FCSTD DOCUMENT  (FreeCAD 0.22R37100 (Git))
Label: composit_stand10_model
License: All rights reserved
LicenseURL: http://en.wikipedia.org/wiki/All_rights_reserved
objects: App::Link×19, App::DocumentObjectGroup×3, PartDesign::CoordinateSystem×1, App::FeaturePython×1, App::Part×1
note: 1 computed .brp shape members not serialized (recipe doc carries the construction recipe); baked Part::Feature solids carry a one-line shape summary decoded from their .brp
EXTERNAL_REF file=composit_stand10.FCStd obj=Local_CS020
EXTERNAL_REF file=composit_stand10.FCStd obj=Body
EXTERNAL_REF file=composit_stand10.FCStd obj=Local_CS007
EXTERNAL_REF file=composit_stand10.FCStd obj=Local_CS010
EXTERNAL_REF file=composit_stand10.FCStd obj=Body001
EXTERNAL_REF file=composit_stand10.FCStd obj=Local_CS004
EXTERNAL_REF file=composit_stand10.FCStd obj=Local_CS005
EXTERNAL_REF file=composit_stand10.FCStd obj=Body012
EXTERNAL_REF file=composit_stand10.FCStd obj=Local_CS006
EXTERNAL_REF file=composit_stand10.FCStd obj=Local_CS012
EXTERNAL_REF file=composit_stand10.FCStd obj=Body003
EXTERNAL_REF file=composit_stand10.FCStd obj=Local_CS009
EXTERNAL_REF file=composit_stand10.FCStd obj=Local_CS015
EXTERNAL_REF file=composit_stand10.FCStd obj=Body010
EXTERNAL_REF file=composit_stand10.FCStd obj=Local_CS008
EXTERNAL_REF file=composit_stand10.FCStd obj=Local_CS013
EXTERNAL_REF file=composit_stand10.FCStd obj=Body006
EXTERNAL_REF file=composit_stand10.FCStd obj=Local_CS014
EXTERNAL_REF file=composit_stand10.FCStd obj=Local_CS016
EXTERNAL_REF file=composit_stand10.FCStd obj=Body004
EXTERNAL_REF file=composit_stand10.FCStd obj=Local_CS018
EXTERNAL_REF file=composit_stand10.FCStd obj=Body014
EXTERNAL_REF file=composit_stand10.FCStd obj=Local_CS025
EXTERNAL_REF file=composit_stand10.FCStd obj=Body011
EXTERNAL_REF file=composit_stand10.FCStd obj=Local_CS026
EXTERNAL_REF file=composit_stand10.FCStd obj=Local_CS027
EXTERNAL_REF file=composit_stand10.FCStd obj=Body019
EXTERNAL_REF file=composit_stand10.FCStd obj=Local_CS028
EXTERNAL_REF file=../magnet_fix.FCStd obj=Local_CS
EXTERNAL_REF file=../magnet_fix.FCStd obj=Body
EXTERNAL_REF file=composit_stand10.FCStd obj=LCS_1
EXTERNAL_REF file=composit_stand10.FCStd obj=Part
EXTERNAL_REF file=composit_stand10.FCStd obj=Local_CS029
EXTERNAL_REF file=composit_stand10.FCStd obj=Local_CS030
EXTERNAL_REF file=composit_stand10.FCStd obj=Body021
EXTERNAL_REF file=composit_stand10.FCStd obj=Local_CS031
EXTERNAL_REF file=composit_stand10.FCStd obj=Body024
EXTERNAL_REF file=../basin_2.FCStd obj=Local_CS
EXTERNAL_REF file=composit_stand10.FCStd obj=Local_CS022
EXTERNAL_REF file=../basin_2.FCStd obj=Body
EXTERNAL_REF file=composit_stand10.FCStd obj=Local_CS033
EXTERNAL_REF file=composit_stand10.FCStd obj=Body008
EXTERNAL_REF file=composit_stand10.FCStd obj=Local_CS032
EXTERNAL_REF file=composit_stand10.FCStd obj=Local_CS034
EXTERNAL_REF file=composit_stand10.FCStd obj=Body028
EXTERNAL_REF file=composit_stand10.FCStd obj=Local_CS035
EXTERNAL_REF file=../water_sensor.FCStd obj=Assembly
EXTERNAL_REF file=../composit_electric_shield.FCStd obj=Body
EXTERNAL_REF file=../composit_electric_shield.FCStd obj=Local_CS
EXTERNAL_REF file=composit_stand10.FCStd obj=Local_CS036

FEATURE [App::DocumentObjectGroup] Parts
FEATURE [PartDesign::CoordinateSystem] LCS_Origin
  AttacherType = Attacher::AttachEngine3D
  AttachmentSupport = -> [XY_Plane]
  MapMode = 2
FEATURE [App::DocumentObjectGroup] Constraints
FEATURE [App::FeaturePython] Variables  # WARN: FeaturePython — macro-defined, semantics opaque (R4)
  Type = App::PropertyContainer
FEATURE [App::DocumentObjectGroup] Configurations
FEATURE [App::Link] face
  AttachedBy = #Local_CS020
  AttachedTo = Parent Assembly#LCS_Origin
  AttachmentOffset = pos=(0,0,0) rot=(0,0,1;3.14159rad)
  LinkPlacement = pos=(0,0,0) rot=(0,0,1;3.14159rad)
  LinkedObject = -> <external composit_stand10.FCStd>#Body
  Placement = pos=(0,0,0) rot=(0,0,1;3.14159rad)
  SolverId = Asm4EE
  expr: Placement = LCS_Origin.Placement * AttachmentOffset * composit_stand10#Local_CS020.Placement ^ -1
FEATURE [App::Link] back
  AttachedBy = #Local_CS010
  AttachedTo = face#Local_CS007
  LinkPlacement = pos=(0,0,0) rot=(0,0,1;3.14159rad)
  LinkedObject = -> <external composit_stand10.FCStd>#Body001
  Placement = pos=(0,0,0) rot=(0,0,1;3.14159rad)
  SolverId = Asm4EE
  expr: Placement = face.Placement * composit_stand10#Local_CS007.Placement * AttachmentOffset * composit_stand10#Local_CS010.Placement ^ -1
FEATURE [App::Link] sink
  AttachedBy = #Local_CS004
  AttachedTo = face#Local_CS005
  LinkPlacement = pos=(-1.1e-14,-90,140) rot=(0,0,1;3.14159rad)
  LinkedObject = -> <external composit_stand10.FCStd>#Body012
  Placement = pos=(-1.1e-14,-90,140) rot=(0,0,1;3.14159rad)
  SolverId = Asm4EE
  expr: Placement = face.Placement * composit_stand10#Local_CS005.Placement * AttachmentOffset * composit_stand10#Local_CS004.Placement ^ -1
FEATURE [App::Link] lamp_holder
  AttachedBy = #Local_CS012
  AttachedTo = face#Local_CS006
  LinkPlacement = pos=(-1.1e-14,-90,254) rot=(0,0,1;3.14159rad)
  LinkedObject = -> <external composit_stand10.FCStd>#Body003
  Placement = pos=(-1.1e-14,-90,254) rot=(0,0,1;3.14159rad)
  SolverId = Asm4EE
  expr: Placement = face.Placement * composit_stand10#Local_CS006.Placement * AttachmentOffset * composit_stand10#Local_CS012.Placement ^ -1
FEATURE [App::Link] cap_outer
  AttachedBy = #Local_CS015
  AttachedTo = face#Local_CS009
  LinkPlacement = pos=(0,0,813) rot=(0,0,1;3.14159rad)
  LinkedObject = -> <external composit_stand10.FCStd>#Body010
  Placement = pos=(0,0,813) rot=(0,0,1;3.14159rad)
  SolverId = Asm4EE
  expr: Placement = face.Placement * composit_stand10#Local_CS009.Placement * AttachmentOffset * composit_stand10#Local_CS015.Placement ^ -1
FEATURE [App::Link] dropper_fix_composit
  AttachedBy = #Local_CS013
  AttachedTo = face#Local_CS008
  LinkPlacement = pos=(-1.1e-14,-90,813.1) rot=(0,0,1;3.14159rad)
  LinkedObject = -> <external composit_stand10.FCStd>#Body006
  Placement = pos=(-1.1e-14,-90,813.1) rot=(0,0,1;3.14159rad)
  SolverId = Asm4EE
  expr: Placement = face.Placement * composit_stand10#Local_CS008.Placement * AttachmentOffset * composit_stand10#Local_CS013.Placement ^ -1
FEATURE [App::Link] dropper_fix_PP
  AttachedBy = #Local_CS016
  AttachedTo = dropper_fix_composit#Local_CS014
  LinkPlacement = pos=(-1.1e-14,-90,816.1) rot=(0,0,1;3.14159rad)
  LinkedObject = -> <external composit_stand10.FCStd>#Body004
  Placement = pos=(-1.1e-14,-90,816.1) rot=(0,0,1;3.14159rad)
  SolverId = Asm4EE
  expr: Placement = dropper_fix_composit.Placement * composit_stand10#Local_CS014.Placement * AttachmentOffset * composit_stand10#Local_CS016.Placement ^ -1
FEATURE [App::Link] bottom_composit
  AttachedBy = #Local_CS018
  AttachedTo = face#Local_CS007
  LinkPlacement = pos=(0,0,0) rot=(0,0,1;3.14159rad)
  LinkedObject = -> <external composit_stand10.FCStd>#Body014
  Placement = pos=(0,0,0) rot=(0,0,1;3.14159rad)
  SolverId = Asm4EE
  expr: Placement = face.Placement * composit_stand10#Local_CS007.Placement * AttachmentOffset * composit_stand10#Local_CS018.Placement ^ -1
FEATURE [App::Link] cap_inner
  AttachedBy = #Local_CS025
  AttachedTo = cap_outer#Local_CS015
  LinkPlacement = pos=(0,0,813) rot=(0,0,1;3.14159rad)
  LinkedObject = -> <external composit_stand10.FCStd>#Body011
  Placement = pos=(0,0,813) rot=(0,0,1;3.14159rad)
  SolverId = Asm4EE
  expr: Placement = cap_outer.Placement * composit_stand10#Local_CS015.Placement * AttachmentOffset * composit_stand10#Local_CS025.Placement ^ -1
FEATURE [App::Link] magnet_fix
  AttachedBy = #Local_CS026
  AttachedTo = face#Local_CS027
  LinkPlacement = pos=(-299.78,-218,16) rot=(0,0,1;3.14159rad)
  LinkedObject = -> <external composit_stand10.FCStd>#Body019
  Placement = pos=(-299.78,-218,16) rot=(0,0,1;3.14159rad)
  SolverId = Asm4EE
  expr: Placement = face.Placement * composit_stand10#Local_CS027.Placement * AttachmentOffset * composit_stand10#Local_CS026.Placement ^ -1
FEATURE [App::Link] Body
  AttachedBy = #Local_CS
  AttachedTo = magnet_fix#Local_CS028
  LinkPlacement = pos=(-299.78,-210.7,36) rot=(-0.707107,0,-0.707107;3.14159rad)
  LinkedObject = -> <external ../magnet_fix.FCStd>#Body
  Placement = pos=(-299.78,-210.7,36) rot=(-0.707107,0,-0.707107;3.14159rad)
  SolverId = Asm4EE
  expr: Placement = magnet_fix.Placement * composit_stand10#Local_CS028.Placement * AttachmentOffset * magnet_fix#Local_CS.Placement ^ -1
FEATURE [App::Link] modules
  AttachedBy = #LCS_1
  AttachedTo = face#Local_CS020
  AttachmentOffset = pos=(0,0,-1.4) rot=(0,0,1;0rad)
  LinkPlacement = pos=(0,0,-1.4) rot=(0,0,1;3.14159rad)
  LinkedObject = -> <external composit_stand10.FCStd>#Part
  Placement = pos=(0,0,-1.4) rot=(0,0,1;3.14159rad)
  SolverId = Asm4EE
  expr: Placement = face.Placement * composit_stand10#Local_CS020.Placement * AttachmentOffset * composit_stand10#LCS_1.Placement ^ -1
FEATURE [App::Link] front_shield
  AttachedBy = #Local_CS029
  AttachedTo = bottom_composit#Local_CS030
  LinkPlacement = pos=(-2.73e-14,-223,6) rot=(0,0,1;3.14159rad)
  LinkedObject = -> <external composit_stand10.FCStd>#Body021
  Placement = pos=(-2.73e-14,-223,6) rot=(0,0,1;3.14159rad)
  SolverId = Asm4EE
  expr: Placement = bottom_composit.Placement * composit_stand10#Local_CS030.Placement * AttachmentOffset * composit_stand10#Local_CS029.Placement ^ -1
FEATURE [App::Link] Body024
  AttachedBy = #Local_CS031
  AttachedTo = face#Local_CS020
  AttachmentOffset = pos=(0,0,6) rot=(0,0,1;0rad)
  LinkPlacement = pos=(0,0,6) rot=(0,0,1;3.14159rad)
  LinkedObject = -> <external composit_stand10.FCStd>#Body024
  Placement = pos=(0,0,6) rot=(0,0,1;3.14159rad)
  SolverId = Asm4EE
  expr: Placement = face.Placement * composit_stand10#Local_CS020.Placement * AttachmentOffset * composit_stand10#Local_CS031.Placement ^ -1
FEATURE [App::Link] Body025
  AttachedBy = #Local_CS
  AttachedTo = bottom_composit#Local_CS022
  AttachmentOffset = pos=(0,0,0) rot=(0,0,1;1.5708rad)
  LinkPlacement = pos=(-1.42e-14,-116.3,11) rot=(0,0,1;4.71239rad)
  LinkedObject = -> <external ../basin_2.FCStd>#Body
  Placement = pos=(-1.42e-14,-116.3,11) rot=(0,0,1;4.71239rad)
  SolverId = Asm4EE
  expr: Placement = bottom_composit.Placement * composit_stand10#Local_CS022.Placement * AttachmentOffset * basin_2#Local_CS.Placement ^ -1
FEATURE [App::Link] pump_holder
  AttachedBy = #Local_CS033
  AttachedTo = Body025#Local_CS
  AttachmentOffset = pos=(0,0,2) rot=(0,0,1;4.71239rad)
  LinkPlacement = pos=(2.89e-14,-19.3,13) rot=(0,0,-1;3.14159rad)
  LinkedObject = -> <external composit_stand10.FCStd>#Body008
  Placement = pos=(2.89e-14,-19.3,13) rot=(0,0,-1;3.14159rad)
  SolverId = Asm4EE
  expr: Placement = Body025.Placement * basin_2#Local_CS.Placement * AttachmentOffset * composit_stand10#Local_CS033.Placement ^ -1
FEATURE [App::Link] Body028
  AttachedBy = #Local_CS034
  AttachedTo = pump_holder#Local_CS032
  LinkPlacement = pos=(-103,-97.3,82) rot=(0,0,-1;3.14159rad)
  LinkedObject = -> <external composit_stand10.FCStd>#Body028
  Placement = pos=(-103,-97.3,82) rot=(0,0,-1;3.14159rad)
  SolverId = Asm4EE
  expr: Placement = pump_holder.Placement * composit_stand10#Local_CS032.Placement * AttachmentOffset * composit_stand10#Local_CS034.Placement ^ -1
FEATURE [App::Link] water_sensor
  AttachedBy = Origin
  AttachedTo = Body028#Local_CS035
  LinkPlacement = pos=(-103,-90.3,81) rot=(0,0,-1;3.14159rad)
  LinkedObject = -> <external ../water_sensor.FCStd>#Assembly
  Placement = pos=(-103,-90.3,81) rot=(0,0,-1;3.14159rad)
  SolverId = Asm4EE
  expr: LinkedObject = <<water_sensor>>#<<Assembly>>._self
  expr: Placement = Body028.Placement * composit_stand10#Local_CS035.Placement * AttachmentOffset
FEATURE [App::Link] composit_electric_shield_inner
  AttachedBy = #Local_CS
  AttachedTo = face#Local_CS036
  LinkPlacement = pos=(-286.163,-80,555.5) rot=(-0.57735,0.57735,0.57735;4.18879rad)
  LinkedObject = -> <external ../composit_electric_shield.FCStd>#Body
  Placement = pos=(-286.163,-80,555.5) rot=(-0.57735,0.57735,0.57735;4.18879rad)
  SolverId = Asm4EE
  expr: LinkedObject = composit_electric_shield#<<composit_electric_shield_inner>>._self
  expr: Placement = face.Placement * composit_stand10#Local_CS036.Placement * AttachmentOffset * composit_electric_shield#Local_CS.Placement ^ -1
FEATURE [App::Part] Assembly
  AssemblyType = Part::Link
  Group = -> [LCS_Origin,Constraints,Variables,Configurations,face,back,sink,lamp_holder,cap_outer,dropper_fix_composit,dropper_fix_PP,bottom_composit,cap_inner,magnet_fix,Body,modules,front_shield,Body024,Body025,pump_holder,Body028,water_sensor,composit_electric_shield_inner]
  Origin = -> Origin
  Type = Assembly

RESOLVED EXTERNAL PARTS (link-assembly join: the EXTERNAL_REF files above that resolve inside this repo's crawl, each included once):
---- part ../basin_2.FCStd = doc fcstd_f6d56c476fde ----
FCSTD DOCUMENT  (FreeCAD 0.22R37100 (Git))
Label: basin_2
License: All rights reserved
LicenseURL: http://en.wikipedia.org/wiki/All_rights_reserved
objects: Sketcher::SketchObject×2, PartDesign::AdditivePipe×1, PartDesign::Pad×1, PartDesign::CoordinateSystem×1, PartDesign::Body×1
note: 8 computed .brp shape members not serialized (recipe doc carries the construction recipe); baked Part::Feature solids carry a one-line shape summary decoded from their .brp

FEATURE [Sketcher::SketchObject] Sketch
  AttachmentOffset = pos=(65,0,0) rot=(0,0,1;0rad)
  AttachmentSupport = -> [XZ_Plane]
  FullyConstrained = true
  MapMode = 5
  Placement = pos=(65,0,0) rot=(1,0,0;1.5708rad)
  expr: .AttachmentOffset.Base.x = <<Sketch001>>.Constraints.width / 2
  sketch-geometry (15):
    g0: LineSegment StartX=2.94242 StartY=2.41503 StartZ=0 EndX=25.2037 EndY=114.39 EndZ=0
    g1: LineSegment StartX=24.2229 StartY=114.585 StartZ=0 EndX=1.96161 EndY=2.61002 EndZ=0
    g2: LineSegment StartX=-6e-16 StartY=0 StartZ=0 EndX=-4e-16 EndY=1 EndZ=0
    g3: ArcOfCircle CenterX=0 CenterY=3 CenterZ=0 NormalX=0 NormalY=0 NormalZ=1 AngleXU=0 Radius=2 StartAngle=4.71239 EndAngle=6.08694
    g4: ArcOfCircle CenterX=0 CenterY=3 CenterZ=0 NormalX=0 NormalY=0 NormalZ=1 AngleXU=0 Radius=3 StartAngle=4.71239 EndAngle=6.08694
    g5: ArcOfCircle CenterX=27.1653 CenterY=114 CenterZ=0 NormalX=0 NormalY=0 NormalZ=1 AngleXU=0 Radius=2 StartAngle=0.523599 EndAngle=2.94535
    g6: LineSegment StartX=28.8974 StartY=115 StartZ=0 EndX=31.567 EndY=110.376 EndZ=0
    g7: LineSegment StartX=29.7634 StartY=115.5 StartZ=0 EndX=32.433 EndY=110.876 EndZ=0
    g8: LineSegment StartX=0 StartY=117 StartZ=0 EndX=27.1653 EndY=117 EndZ=0
    g9: LineSegment StartX=27.1653 StartY=117 StartZ=0 EndX=27.1653 EndY=0 EndZ=0
    g10: ArcOfCircle CenterX=27.1653 CenterY=114 CenterZ=0 NormalX=0 NormalY=0 NormalZ=1 AngleXU=0 Radius=3 StartAngle=0.523599 EndAngle=1.5708
    g11: ArcOfCircle CenterX=27.1653 CenterY=114 CenterZ=0 NormalX=0 NormalY=0 NormalZ=1 AngleXU=0 Radius=3 StartAngle=1.5708 EndAngle=2.94535
    g12: LineSegment StartX=32.5 StartY=0 StartZ=0 EndX=32.5 EndY=110.626 EndZ=0
    g13: ArcOfCircle CenterX=32 CenterY=110.626 CenterZ=0 NormalX=0 NormalY=0 NormalZ=1 AngleXU=0 Radius=0.5 StartAngle=3.66519 EndAngle=6.28319
    g14: ArcOfCircle CenterX=32 CenterY=110.626 CenterZ=0 NormalX=0 NormalY=0 NormalZ=1 AngleXU=0 Radius=0.5 StartAngle=-9.8e-15 EndAngle=0.523599
  constraints (39):
    c: Coincident(g-1,g2)
    c: PointOnObject(g2,g-2)
    c: PointOnObject(g3,g-2)
    c: Coincident(g3,g2)
    c: Coincident(g4,g3)
    c: Coincident(g4,g2)
    c: Tangent(g4,g0) = -1.5708
    c: Tangent(g3,g1) = 1.5708
    c: DistanceY(g2,g2) = 1
    c: Parallel(g1,g0)
    c: Coincident(g10,g5)
    c: Tangent(g5,g0) = 1.5708
    c: Tangent(g11,g1) = -1.5708
    c: Tangent(g6,g5) = 1.5708
    c: Tangent(g6,g13) = -1.5708
    c: Tangent(g7,g10) = 1.5708
    c: Tangent(g7,g14) = 1.5708
    c: Parallel(g6,g7)
    c: PointOnObject(g8,g-2)
    c: Horizontal(g8)
    c: Coincident(g8,g9)
    c: PointOnObject(g9,g-1)
    c: Vertical(g9)
    c: DistanceY(g8) = 117
    c: Distance(g8,g13) = 8
    c: Angle(g7) = -1.0472
    c: DistanceX(g8) = 27.1653
    c: Radius(g3) = 2
    c: Coincident(g10,g11)
    c: Coincident(g10,g11)
    c: Radius(g10) = 3
    c: Tangent(g8,g10) = 1.5708
    c: PointOnObject(g10,g9)
    c: PointOnObject(g12,g-1)
    c: Coincident(g13,g14)
    c: Coincident(g13,g14)
    c: Tangent(g12,g13) = -1.5708
    c: Vertical(g12)
    c: DistanceX(g13) = 32.5
FEATURE [Sketcher::SketchObject] Sketch001
  AttachmentSupport = -> [XY_Plane]
  FullyConstrained = true
  MapMode = 5
  sketch-geometry (10):
    g0: LineSegment StartX=-63 StartY=-163 StartZ=0 EndX=63 EndY=-163 EndZ=0
    g1: LineSegment StartX=65 StartY=-161 StartZ=0 EndX=65 EndY=161 EndZ=0
    g2: LineSegment StartX=63 StartY=163 StartZ=0 EndX=-63 EndY=163 EndZ=0
    g3: LineSegment StartX=-65 StartY=161 StartZ=0 EndX=-65 EndY=-161 EndZ=0
    g4: ArcOfCircle CenterX=-63 CenterY=-161 CenterZ=0 NormalX=0 NormalY=0 NormalZ=1 AngleXU=0 Radius=2 StartAngle=3.14159 EndAngle=4.71239
    g5: ArcOfCircle CenterX=63 CenterY=-161 CenterZ=0 NormalX=0 NormalY=0 NormalZ=1 AngleXU=0 Radius=2 StartAngle=4.71239 EndAngle=6.28319
    g6: ArcOfCircle CenterX=63 CenterY=161 CenterZ=0 NormalX=0 NormalY=0 NormalZ=1 AngleXU=0 Radius=2 StartAngle=2.7e-15 EndAngle=1.5708
    g7: ArcOfCircle CenterX=-63 CenterY=161 CenterZ=0 NormalX=0 NormalY=0 NormalZ=1 AngleXU=0 Radius=2 StartAngle=1.5708 EndAngle=3.14159
    g8: GeomPoint X=-65 Y=-163 Z=0
    g9: GeomPoint X=65 Y=163 Z=0
  constraints (23):
    c: Tangent(g0,g4) = -1.5708
    c: Tangent(g0,g5) = -1.5708
    c: Tangent(g1,g5) = -1.5708
    c: Tangent(g1,g6) = -1.5708
    c: Tangent(g2,g6) = -1.5708
    c: Tangent(g2,g7) = -1.5708
    c: Tangent(g3,g7) = -1.5708
    c: Tangent(g3,g4) = -1.5708
    c: Horizontal(g0)
    c: Horizontal(g2)
    c: Vertical(g1)
    c: Vertical(g3)
    c: Equal(g4,g5)
    c: Equal(g5,g6)
    c: Equal(g6,g7)
    c: PointOnObject(g8,g0)
    c: PointOnObject(g8,g3)
    c: PointOnObject(g9,g1)
    c: PointOnObject(g9,g2)
    c: Symmetric(g8,g9,g-1)
    c: DistanceX(g8,g9) = 130  'width'
    c: DistanceY(g8,g9) = 326  'length'
    c: Radius(g6) = 2
FEATURE [PartDesign::AdditivePipe] AdditivePipe
  AuxilleryCurvelinear = true
  AuxillerySpineTangent = false
  Binormal = (0,0,0)
  Mode = 0
  Placement = pos=(0,0,0) rot=(1,0,0;1.5708rad)
  Profile = -> Sketch
  Spine = -> Sketch001
  SpineTangent = false
  Suppressed = false
  Transformation = 0
  Transition = 0
FEATURE [PartDesign::Pad] Pad
  BaseFeature = -> AdditivePipe
  Direction = (0,0,1)
  Length = 1
  Length2 = 10
  Placement = pos=(0,0,0) rot=(1,0,0;1.5708rad)
  Profile = -> Sketch001
  ReferenceAxis = -> Sketch001 [N_Axis]
  Suppressed = false
  Type = 0
FEATURE [PartDesign::CoordinateSystem] Local_CS
  AttacherType = Attacher::AttachEngine3D
  AttachmentSupport = -> [XY_Plane]
  MapMode = 5
FEATURE [PartDesign::Body] Body
  Group = -> [Sketch,Sketch001,AdditivePipe,Pad,Local_CS]
  Origin = -> Origin
  Tip = -> Pad
---- part ../composit_electric_shield.FCStd = doc fcstd_7e5574ddc39a (52053 chars; too large to inline — full recipe in that document) ----
---- part ../magnet_fix.FCStd = doc fcstd_efc328589249 ----
FCSTD DOCUMENT  (FreeCAD 0.22R37100 (Git))
Label: magnet_fix
License: All rights reserved
LicenseURL: http://en.wikipedia.org/wiki/All_rights_reserved
objects: Sketcher::SketchObject×10, PartDesign::SubShapeBinder×4, PartDesign::Pad×4, TechDraw::DrawViewDimension×3, PartDesign::Body×2, TechDraw::DrawViewPart×2, PartDesign::Pocket×1, Spreadsheet::Sheet×1, PartDesign::CoordinateSystem×1, PartDesign::LinearPattern×1, Part::Mirroring×1, Part::FeaturePython×1, Part::Extrusion×1, Part::Compound×1, PartDesign::Boolean×1, Part::Feature×1, TechDraw::DrawSVGTemplate×1, TechDraw::DrawPage×1
note: 39 computed .brp shape members not serialized (recipe doc carries the construction recipe); baked Part::Feature solids carry a one-line shape summary decoded from their .brp

FEATURE [Sketcher::SketchObject] Sketch
  FullyConstrained = true
  sketch-geometry (5):
    g0: LineSegment StartX=-20.65 StartY=-7.3 StartZ=0 EndX=20.65 EndY=-7.3 EndZ=0
    g1: LineSegment StartX=20.65 StartY=-7.3 StartZ=0 EndX=20.65 EndY=7.3 EndZ=0
    g2: LineSegment StartX=20.65 StartY=7.3 StartZ=0 EndX=-20.65 EndY=7.3 EndZ=0
    g3: LineSegment StartX=-20.65 StartY=7.3 StartZ=0 EndX=-20.65 EndY=-7.3 EndZ=0
    g4: GeomPoint X=0 Y=0 Z=0
  constraints (12):
    c: Coincident(g0,g1)
    c: Coincident(g1,g2)
    c: Coincident(g2,g3)
    c: Coincident(g3,g0)
    c: Horizontal(g0)
    c: Horizontal(g2)
    c: Vertical(g1)
    c: Vertical(g3)
    c: Symmetric(g2,g0,g4)
    c: Coincident(g4,g-1)
    c: DistanceX(g0,g1) = 41.3
    c: DistanceY(g0,g1) = 14.6
FEATURE [Sketcher::SketchObject] Sketch001
  ExternalGeometry = -> [Sketch]
  FullyConstrained = true
  sketch-geometry (5):
    g0: LineSegment StartX=-14.1 StartY=-7.3 StartZ=0 EndX=14.1 EndY=-7.3 EndZ=0
    g1: LineSegment StartX=14.1 StartY=-7.3 StartZ=0 EndX=14.1 EndY=7.3 EndZ=0
    g2: LineSegment StartX=14.1 StartY=7.3 StartZ=0 EndX=-14.1 EndY=7.3 EndZ=0
    g3: LineSegment StartX=-14.1 StartY=7.3 StartZ=0 EndX=-14.1 EndY=-7.3 EndZ=0
    g4: GeomPoint X=0 Y=0 Z=0
  constraints (12):
    c: Coincident(g0,g1)
    c: Coincident(g1,g2)
    c: Coincident(g2,g3)
    c: Coincident(g3,g0)
    c: Horizontal(g0)
    c: Horizontal(g2)
    c: Vertical(g1)
    c: Vertical(g3)
    c: Symmetric(g2,g0,g4)
    c: Coincident(g4,g-1)
    c: Horizontal(g1,g-3)
    c: DistanceX(g2,g2) = 28.2
FEATURE [Sketcher::SketchObject] Sketch002  label="holes"
  FullyConstrained = true
  sketch-geometry (10):
    g0: ArcOfCircle CenterX=17 CenterY=-1.85 CenterZ=0 NormalX=0 NormalY=0 NormalZ=1 AngleXU=0 Radius=1.4 StartAngle=3.14159 EndAngle=6.28319
    g1: ArcOfCircle CenterX=17 CenterY=1.85 CenterZ=0 NormalX=0 NormalY=0 NormalZ=1 AngleXU=0 Radius=1.4 StartAngle=0 EndAngle=3.14159
    g2: LineSegment StartX=15.6 StartY=-1.85 StartZ=0 EndX=15.6 EndY=1.85 EndZ=0
    g3: LineSegment StartX=18.4 StartY=-1.85 StartZ=0 EndX=18.4 EndY=1.85 EndZ=0
    g4: ArcOfCircle CenterX=-17 CenterY=-1.85 CenterZ=0 NormalX=0 NormalY=0 NormalZ=1 AngleXU=0 Radius=1.4 StartAngle=3.14159 EndAngle=6.28319
    g5: ArcOfCircle CenterX=-17 CenterY=1.85 CenterZ=0 NormalX=0 NormalY=0 NormalZ=1 AngleXU=0 Radius=1.4 StartAngle=0 EndAngle=3.14159
    g6: LineSegment StartX=-18.4 StartY=-1.85 StartZ=0 EndX=-18.4 EndY=1.85 EndZ=0
    g7: LineSegment StartX=-15.6 StartY=-1.85 StartZ=0 EndX=-15.6 EndY=1.85 EndZ=0
    g8: GeomPoint X=17 Y=-3.25 Z=0
    g9: GeomPoint X=17 Y=3.25 Z=0
  constraints (22):
    c: Tangent(g0,g2) = 1.5708
    c: Tangent(g0,g3) = -1.5708
    c: Tangent(g1,g2) = 1.5708
    c: Tangent(g1,g3) = -1.5708
    c: Equal(g0,g1)
    c: Vertical(g3)
    c: Tangent(g4,g6) = 1.5708
    c: Tangent(g4,g7) = -1.5708
    c: Tangent(g5,g6) = 1.5708
    c: Tangent(g5,g7) = -1.5708
    c: Equal(g4,g5)
    c: Vertical(g6)
    c: PointOnObject(g8,g0)
    c: PointOnObject(g9,g1)
    c: Vertical(g9,g0)
    c: Symmetric(g8,g9,g-1)
    c: DistanceY(g8,g9) = 6.5
    c: DistanceX(g0,g0) = 2.8
    c: Symmetric(g4,g1,g-1)
    c: Equal(g7,g2)
    c: Equal(g5,g1)
    c: DistanceX(g4,g0) = 34
FEATURE [PartDesign::SubShapeBinder] Binder
  BindCopyOnChange = 0
  BindMode = 0
  ClaimChildren = false
  Context = -> Body [Binder.]
  Fuse = false
  MakeFace = true
  OffsetFill = false
  OffsetIntersection = false
  OffsetJoinType = 0
  OffsetOpenResult = false
  PartialLoad = false
  Relative = true
  Support = -> [Sketch]
  _Version = 2
FEATURE [PartDesign::Pad] Pad
  Direction = (0,0,1)
  Length = 3.5
  Length2 = 10
  Profile = -> Binder
  Suppressed = false
  Type = 0
FEATURE [PartDesign::SubShapeBinder] Binder001
  BindCopyOnChange = 0
  BindMode = 0
  ClaimChildren = false
  Context = -> Body [Binder001.]
  Fuse = false
  MakeFace = true
  OffsetFill = false
  OffsetIntersection = false
  OffsetJoinType = 0
  OffsetOpenResult = false
  PartialLoad = false
  Relative = true
  Support = -> [Sketch001]
  _Version = 2
FEATURE [PartDesign::Pad] Pad001
  BaseFeature = -> Pad
  Direction = (0,0,1)
  Length = 12.6
  Length2 = 10
  Profile = -> Binder001
  Suppressed = false
  Type = 0
FEATURE [PartDesign::SubShapeBinder] Binder002
  BindCopyOnChange = 0
  BindMode = 0
  ClaimChildren = false
  Context = -> Body [Binder002.]
  Fuse = false
  MakeFace = true
  OffsetFill = false
  OffsetIntersection = false
  OffsetJoinType = 0
  OffsetOpenResult = false
  PartialLoad = false
  Relative = true
  Support = -> [Sketch002]
  _Version = 2
FEATURE [PartDesign::Pocket] Pocket
  BaseFeature = -> Pad001
  Direction = (0,0,-1)
  Length = 5
  Length2 = 5
  Midplane = true
  Profile = -> Binder002
  Suppressed = false
  Type = 1
FEATURE [Sketcher::SketchObject] Sketch003
  ExternalGeometry = -> [Sketch001]
  FullyConstrained = true
  sketch-geometry (5):
    g0: LineSegment StartX=-10.75 StartY=7.3 StartZ=0 EndX=10.75 EndY=7.3 EndZ=0
    g1: LineSegment StartX=10.75 StartY=7.3 StartZ=0 EndX=10.75 EndY=9.3 EndZ=0
    g2: LineSegment StartX=10.75 StartY=9.3 StartZ=0 EndX=-10.75 EndY=9.3 EndZ=0
    g3: LineSegment StartX=-10.75 StartY=9.3 StartZ=0 EndX=-10.75 EndY=7.3 EndZ=0
    g4: GeomPoint X=0 Y=8.3 Z=0
  constraints (13):
    c: Coincident(g0,g1)
    c: Coincident(g1,g2)
    c: Coincident(g2,g3)
    c: Coincident(g3,g0)
    c: Horizontal(g0)
    c: Horizontal(g2)
    c: Vertical(g1)
    c: Vertical(g3)
    c: PointOnObject(g4,g-2)
    c: Symmetric(g0,g1,g4)
    c: DistanceX(g0,g0) = 21.5
    c: PointOnObject(g0,g-3)
    c: DistanceY(g1,g1) = 2
FEATURE [Spreadsheet::Sheet] Spreadsheet  label="Properties"
  cells = B2(length)==41.3 mm; C2(width)==16.6 mm
FEATURE [PartDesign::CoordinateSystem] Local_CS
  AttacherType = Attacher::AttachEngine3D
  AttachmentSupport = -> [XY_Plane]
  MapMode = 5
FEATURE [Sketcher::SketchObject] Sketch004
  AttachmentOffset = pos=(0,0,4) rot=(0,0,1;0rad)
  AttachmentSupport = -> [XY_Plane]
  FullyConstrained = true
  MapMode = 5
  Placement = pos=(0,0,4) rot=(0,0,1;0rad)
  sketch-geometry (4):
    g0: LineSegment StartX=-10.75 StartY=7.3 StartZ=0 EndX=10.75 EndY=7.3 EndZ=0
    g1: LineSegment StartX=10.75 StartY=7.3 StartZ=0 EndX=10.75 EndY=9.3 EndZ=0
    g2: LineSegment StartX=10.75 StartY=9.3 StartZ=0 EndX=-10.75 EndY=9.3 EndZ=0
    g3: LineSegment StartX=-10.75 StartY=9.3 StartZ=0 EndX=-10.75 EndY=7.3 EndZ=0
  constraints (11):
    c: Coincident(g0,g1)
    c: Coincident(g1,g2)
    c: Coincident(g2,g3)
    c: Coincident(g3,g0)
    c: Horizontal(g0)
    c: Vertical(g1)
    c: Vertical(g3)
    c: DistanceY(g1,g1) = 2
    c: DistanceY(g0) = 7.3
    c: Symmetric(g2,g1,g-2)
    c: DistanceX(g0,g0) = 21.5
FEATURE [PartDesign::Pad] Pad002
  BaseFeature = -> Pocket
  Direction = (0,0,1)
  Length = 1
  Length2 = 10
  Profile = -> Sketch004
  ReferenceAxis = -> Sketch004 [N_Axis]
  Suppressed = false
  Type = 0
FEATURE [PartDesign::LinearPattern] LinearPattern
  BaseFeature = -> Pad002
  Direction = -> Z_Axis
  Length = 5
  Mode = 0
  Occurrences = 2
  Offset = 5
  Originals = -> [Pad002]
  Refine = true
  Suppressed = false
FEATURE [PartDesign::Body] Body
  Group = -> [Binder,Pad,Binder001,Pad001,Binder002,Pocket,Local_CS,Sketch004,Pad002,LinearPattern]
  Origin = -> Origin
  Tip = -> LinearPattern
FEATURE [Sketcher::SketchObject] Sketch006  label="magnet_fix_reply_holes"
  ExternalGeometry = -> [Sketch003]
  FullyConstrained = true
  sketch-geometry (2):
    g0: Circle CenterX=18.75 CenterY=0 CenterZ=0 NormalX=0 NormalY=0 NormalZ=1 AngleXU=0 Radius=1.7
    g1: Circle CenterX=-18.75 CenterY=0 CenterZ=0 NormalX=0 NormalY=0 NormalZ=1 AngleXU=0 Radius=1.7
  constraints (5):
    c: PointOnObject(g0,g-1)
    c: Symmetric(g0,g1,g-2)
    c: Equal(g1,g0)
    c: Diameter(g1) = 3.4
    c: DistanceX(g-3,g0) = 8
FEATURE [Sketcher::SketchObject] Sketch005
  ExternalGeometry = -> [Sketch006]
  FullyConstrained = true
  sketch-geometry (3):
    g0: ArcOfCircle CenterX=18.75 CenterY=0 CenterZ=0 NormalX=0 NormalY=0 NormalZ=1 AngleXU=0 Radius=5 StartAngle=4.71239 EndAngle=7.85398
    g1: LineSegment StartX=0 StartY=5 StartZ=0 EndX=18.75 EndY=5 EndZ=0
    g2: LineSegment StartX=0 StartY=-5 StartZ=0 EndX=18.75 EndY=-5 EndZ=0
  constraints (8):
    c: PointOnObject(g1,g-2)
    c: Horizontal(g1)
    c: PointOnObject(g2,g-2)
    c: Horizontal(g2)
    c: Tangent(g2,g0) = -1.5708
    c: Tangent(g1,g0) = 1.5708
    c: Coincident(g0,g-3)
    c: DistanceY(g2,g1) = 10
FEATURE [Part::Mirroring] Part__Mirroring  label="Sketch005 (Mirror #1)"
  Base = (0,0,0)
  Normal = (1,0,0)
  Source = -> Sketch005
FEATURE [Part::FeaturePython] Connect  # WARN: FeaturePython — macro-defined, semantics opaque (R4)
  Objects = -> [Sketch005,Part__Mirroring]
  Tolerance = 0
FEATURE [PartDesign::SubShapeBinder] Binder003
  BindCopyOnChange = 0
  BindMode = 0
  ClaimChildren = true
  Context = -> Body001 [Binder003.]
  Fuse = false
  MakeFace = true
  OffsetFill = false
  OffsetIntersection = false
  OffsetJoinType = 0
  OffsetOpenResult = false
  PartialLoad = false
  Relative = false
  Support = -> [Connect]
  _Version = 2
FEATURE [PartDesign::Pad] Pad003
  Direction = (0,0,1)
  Length = 1
  Length2 = 10
  Profile = -> Binder003
  Refine = true
  Suppressed = false
  Type = 0
FEATURE [Part::Extrusion] Extrude
  Base = -> Sketch006
  Dir = (0,0,1)
  DirMode = 2
  FaceMakerClass = Part::FaceMakerBullseye
  LengthFwd = 10
  LengthRev = 0
  Solid = true
  Symmetric = false
FEATURE [Part::Compound] Compound
  Links = -> [Extrude]
FEATURE [PartDesign::Boolean] Boolean
  BaseFeature = -> Pad003
  Group = -> [Compound]
  Suppressed = false
  Type = 1
  UsePlacement = true
FEATURE [PartDesign::Body] Body001  label="magnet_fix_reply"
  Group = -> [Binder003,Pad003,Boolean]
  Origin = -> Origin001
  Tip = -> Boolean
FEATURE [Part::Feature] Unfold
  shape: bbox 47.5 x 10 x 1 mm, 8 faces (baked)
FEATURE [Sketcher::SketchObject] Unfold_Sketch
  FullyConstrained = false
  sketch-geometry (6):
    g0: ArcOfCircle CenterX=-18.75 CenterY=0 CenterZ=0 NormalX=0 NormalY=0 NormalZ=1 AngleXU=-3.14159 Radius=5 StartAngle=4.71239 EndAngle=7.85398
    g1: LineSegment StartX=18.75 StartY=5 StartZ=0 EndX=-18.75 EndY=5 EndZ=0
    g2: LineSegment StartX=-18.75 StartY=-5 StartZ=0 EndX=18.75 EndY=-5 EndZ=0
    g3: ArcOfCircle CenterX=18.75 CenterY=0 CenterZ=0 NormalX=0 NormalY=0 NormalZ=1 AngleXU=0 Radius=5 StartAngle=4.71239 EndAngle=7.85398
    g4: Circle CenterX=-18.75 CenterY=0 CenterZ=0 NormalX=0 NormalY=0 NormalZ=-1 AngleXU=-3.14159 Radius=1.7
    g5: Circle CenterX=18.75 CenterY=0 CenterZ=0 NormalX=0 NormalY=0 NormalZ=-1 AngleXU=-3.14159 Radius=1.7
FEATURE [Sketcher::SketchObject] Unfold_Sketch_Outline
  FullyConstrained = false
  sketch-geometry (4):
    g0: ArcOfCircle CenterX=-18.75 CenterY=0 CenterZ=0 NormalX=0 NormalY=0 NormalZ=1 AngleXU=-3.14159 Radius=5 StartAngle=4.71239 EndAngle=7.85398
    g1: LineSegment StartX=-18.75 StartY=-5 StartZ=0 EndX=18.75 EndY=-5 EndZ=0
    g2: ArcOfCircle CenterX=18.75 CenterY=0 CenterZ=0 NormalX=0 NormalY=0 NormalZ=1 AngleXU=0 Radius=5 StartAngle=4.71239 EndAngle=7.85398
    g3: LineSegment StartX=18.75 StartY=5 StartZ=0 EndX=-18.75 EndY=5 EndZ=0
FEATURE [Sketcher::SketchObject] Unfold_Sketch_Internal
  FullyConstrained = false
  sketch-geometry (2):
    g0: Circle CenterX=18.75 CenterY=0 CenterZ=0 NormalX=0 NormalY=0 NormalZ=-1 AngleXU=-3.14159 Radius=1.7
    g1: Circle CenterX=-18.75 CenterY=0 CenterZ=0 NormalX=0 NormalY=0 NormalZ=-1 AngleXU=-3.14159 Radius=1.7
FEATURE [TechDraw::DrawSVGTemplate] Template
  Height = 210
  Orientation = 1
  Template = <path>
  Width = 297
FEATURE [TechDraw::DrawViewPart] View
  CoarseView = false
  Direction = (0,0,1)
  Focus = 100
  HardHidden = false
  IsoCount = 0
  IsoHidden = false
  IsoVisible = false
  LockPosition = false
  Perspective = false
  Rotation = 0
  Scale = 4
  ScaleType = 2
  ScrubCount = 0
  SeamHidden = false
  SeamVisible = true
  SmoothHidden = false
  SmoothVisible = true
  Source = -> [Body001]
  X = 112.5
  XDirection = (1,0,0)
  Y = 45
FEATURE [TechDraw::DrawViewPart] View001
  CoarseView = false
  Direction = (0.57735,-0.57735,0.57735)
  Focus = 100
  HardHidden = false
  IsoCount = 0
  IsoHidden = false
  IsoVisible = false
  LockPosition = false
  Perspective = false
  Rotation = 0
  Scale = 4
  ScaleType = 2
  ScrubCount = 0
  SeamHidden = false
  SeamVisible = true
  SmoothHidden = false
  SmoothVisible = true
  Source = -> [Body001]
  X = 208.5
  XDirection = (0.707107,0.707107,0)
  Y = 135
FEATURE [TechDraw::DrawViewDimension] Dimension
  AngleOverride = false
  Arbitrary = false
  ArbitraryTolerances = false
  BoxCorners = (2) [(-95,-20,0),(95,20,0)]
  EqualTolerance = true
  ExtensionAngle = 0
  FormatSpec = %.2w
  FormatSpecOverTolerance = %+.2w
  FormatSpecUnderTolerance = %+.2w
  Inverted = false
  LineAngle = 0
  LockPosition = false
  MeasureType = 1
  OverTolerance = 0
  References2D = -> [View]
  Rotation = 0
  ScaleType = 0
  TheoreticalExact = false
  Type = 1
  UnderTolerance = 0
  X = 0.61437
  Y = 32.297
FEATURE [TechDraw::DrawViewDimension] Dimension001
  AngleOverride = false
  Arbitrary = false
  ArbitraryTolerances = false
  BoxCorners = (2) [(-95,-20,0),(95,20,0)]
  EqualTolerance = true
  ExtensionAngle = 0
  FormatSpec = %.2w
  FormatSpecOverTolerance = %+.2w
  FormatSpecUnderTolerance = %+.2w
  Inverted = false
  LineAngle = 0
  LockPosition = false
  MeasureType = 1
  OverTolerance = 0
  References2D = -> [View]
  Rotation = 0
  ScaleType = 0
  TheoreticalExact = false
  Type = 2
  UnderTolerance = 0
  X = 110.554
  Y = -0.759103
FEATURE [TechDraw::DrawViewDimension] Dimension002
  AngleOverride = false
  Arbitrary = false
  ArbitraryTolerances = false
  BoxCorners = (2) [(-95,-20,0),(95,20,0)]
  EqualTolerance = true
  ExtensionAngle = 0
  FormatSpec = R%.2w
  FormatSpecOverTolerance = %+.2w
  FormatSpecUnderTolerance = %+.2w
  Inverted = false
  LineAngle = 0
  LockPosition = false
  MeasureType = 1
  OverTolerance = 0
  References2D = -> [View]
  Rotation = 0
  ScaleType = 0
  TheoreticalExact = false
  Type = 4
  UnderTolerance = 0
  X = -53.9727
  Y = 5.80719
FEATURE [TechDraw::DrawPage] Page
  KeepUpdated = true
  NextBalloonIndex = 1
  ProjectionType = 0
  Template = -> Template
  Views = -> [View,View001,Dimension,Dimension001,Dimension002]
note: 1 file-system path scrubbed to <path> (originals preserved in the JSON sidecar)
---- part ../water_sensor.FCStd = doc fcstd_5f56f8e384e0 ----
FCSTD DOCUMENT  (FreeCAD 0.22R37100 (Git))
Label: water_sensor
License: All rights reserved
LicenseURL: http://en.wikipedia.org/wiki/All_rights_reserved
objects: PartDesign::CoordinateSystem×9, Sketcher::SketchObject×6, PartDesign::Body×5, App::Link×5, App::Part×5, App::FeaturePython×5, Part::FeaturePython×4, PartDesign::Pad×3, PartDesign::Revolution×2, PartDesign::Mirrored×2, App::AnnotationLabel×2, PartDesign::AdditiveTorus×1, PartDesign::Pocket×1, Assembly::JointGroup×1, Assembly::AssemblyObject×1, App::DocumentObjectGroup×1
note: 40 computed .brp shape members not serialized (recipe doc carries the construction recipe); baked Part::Feature solids carry a one-line shape summary decoded from their .brp

FEATURE [Sketcher::SketchObject] Sketch
  AttachmentSupport = -> [XZ_Plane]
  FullyConstrained = true
  MapMode = 5
  Placement = pos=(0,0,0) rot=(1,0,0;1.5708rad)
  sketch-geometry (6):
    g0: LineSegment StartX=4.75 StartY=0 StartZ=0 EndX=4.75 EndY=12 EndZ=0
    g1: LineSegment StartX=4.75 StartY=12 StartZ=0 EndX=7.9 EndY=12 EndZ=0
    g2: LineSegment StartX=10.9 StartY=9 StartZ=0 EndX=11.8 EndY=9 EndZ=0
    g3: LineSegment StartX=11.8 StartY=9 StartZ=0 EndX=11.8 EndY=0 EndZ=0
    g4: LineSegment StartX=11.8 StartY=0 StartZ=0 EndX=4.75 EndY=0 EndZ=0
    g5: ArcOfCircle CenterX=7.9 CenterY=9 CenterZ=0 NormalX=0 NormalY=0 NormalZ=1 AngleXU=0 Radius=3 StartAngle=1e-16 EndAngle=1.5708
  constraints (17):
    c: PointOnObject(g0,g-1)
    c: Vertical(g0)
    c: Coincident(g0,g1)
    c: Horizontal(g1)
    c: Horizontal(g2)
    c: Coincident(g2,g3)
    c: PointOnObject(g3,g-1)
    c: Vertical(g3)
    c: Coincident(g3,g4)
    c: Coincident(g4,g0)
    c: Tangent(g1,g5) = 1.5708
    c: Perpendicular(g5,g2) = 4.71239
    c: DistanceX(g0) = 4.75
    c: DistanceY(g0) = 12
    c: DistanceY(g3,g3) = 9
    c: DistanceX(g2) = 10.9
    c: DistanceX(g3) = 11.8
FEATURE [PartDesign::Revolution] Revolution
  Angle = 360
  Angle2 = 60
  Axis = (0,2e-16,1)
  Base = (0,0,0)
  Placement = pos=(0,0,0) rot=(1,0,0;1.5708rad)
  Profile = -> Sketch
  ReferenceAxis = -> Sketch [V_Axis]
  Reversed = true
  Suppressed = false
  Type = 0
FEATURE [PartDesign::Mirrored] Mirrored
  BaseFeature = -> Revolution
  MirrorPlane = -> Sketch [H_Axis]
  Originals = -> [Revolution]
  Placement = pos=(0,0,0) rot=(1,0,0;1.5708rad)
  Refine = true
  Suppressed = false
FEATURE [Sketcher::SketchObject] Sketch001
  AttachmentSupport = -> [XZ_Plane001]
  FullyConstrained = true
  MapMode = 5
  Placement = pos=(0,0,0) rot=(1,0,0;1.5708rad)
  sketch-geometry (14):
    g0: LineSegment StartX=0 StartY=0 StartZ=0 EndX=3.9 EndY=0 EndZ=0
    g1: LineSegment StartX=3.9 StartY=0 StartZ=0 EndX=3.9 EndY=2 EndZ=0
    g2: LineSegment StartX=3.9 StartY=2 StartZ=0 EndX=3.475 EndY=2 EndZ=0
    g3: LineSegment StartX=3.475 StartY=2 StartZ=0 EndX=3.475 EndY=3 EndZ=0
    g4: LineSegment StartX=3.475 StartY=3 StartZ=0 EndX=3.9 EndY=3 EndZ=0
    g5: LineSegment StartX=3.9 StartY=3 StartZ=0 EndX=3.9 EndY=43.6 EndZ=0
    g6: LineSegment StartX=3.9 StartY=43.6 StartZ=0 EndX=5.75 EndY=43.6 EndZ=0
    g7: LineSegment StartX=5.75 StartY=43.6 StartZ=0 EndX=5.75 EndY=51 EndZ=0
    g8: LineSegment StartX=5.75 StartY=51 StartZ=0 EndX=7.625 EndY=51 EndZ=0
    g9: LineSegment StartX=7.625 StartY=51 StartZ=0 EndX=7.625 EndY=52 EndZ=0
    g10: LineSegment StartX=7.625 StartY=52 StartZ=0 EndX=4.9 EndY=52 EndZ=0
    g11: LineSegment StartX=4.9 StartY=52 StartZ=0 EndX=4.9 EndY=66.6 EndZ=0
    g12: LineSegment StartX=4.9 StartY=66.6 StartZ=0 EndX=0 EndY=66.6 EndZ=0
    g13: LineSegment StartX=0 StartY=66.6 StartZ=0 EndX=0 EndY=0 EndZ=0
  constraints (41):
    c: Coincident(g-1,g0)
    c: PointOnObject(g0,g-1)
    c: Coincident(g0,g1)
    c: Vertical(g1)
    c: Coincident(g1,g2)
    c: Horizontal(g2)
    c: Coincident(g2,g3)
    c: Vertical(g3)
    c: Coincident(g3,g4)
    c: Horizontal(g4)
    c: Coincident(g4,g5)
    c: Vertical(g5)
    c: Coincident(g5,g6)
    c: Horizontal(g6)
    c: Coincident(g6,g7)
    c: Vertical(g7)
    c: Coincident(g7,g8)
    c: Horizontal(g8)
    c: Coincident(g8,g9)
    c: Vertical(g9)
    c: Coincident(g9,g10)
    c: Coincident(g10,g11)
    c: Vertical(g11)
    c: Coincident(g11,g12)
    c: PointOnObject(g12,g-2)
    c: Horizontal(g12)
    c: Coincident(g13,g12)
    c: Coincident(g13,g0)
    c: DistanceY(g1) = 2
    c: Vertical(g1,g4)
    c: DistanceX(g0) = 3.9
    c: DistanceX(g2) = 3.475
    c: DistanceY(g3,g3) = 1
    c: DistanceY(g5) = 43.6
    c: DistanceX(g6) = 5.75
    c: Horizontal(g10)
    c: DistanceY(g9,g9) = 1
    c: DistanceY(g9) = 52
    c: DistanceX(g8) = 7.625
    c: DistanceX(g10) = 4.9
    c: DistanceY(g12) = 66.6
FEATURE [PartDesign::Revolution] Revolution001
  Angle = 360
  Angle2 = 60
  Axis = (0,2e-16,1)
  Base = (0,0,0)
  Placement = pos=(0,0,0) rot=(1,0,0;1.5708rad)
  Profile = -> Sketch001
  ReferenceAxis = -> Sketch001 [V_Axis]
  Reversed = true
  Suppressed = false
  Type = 0
FEATURE [Sketcher::SketchObject] Sketch002
  AttachmentSupport = -> [XY_Plane002]
  FullyConstrained = true
  MapMode = 5
  sketch-geometry (4):
    g0: ArcOfCircle CenterX=0 CenterY=0 CenterZ=0 NormalX=0 NormalY=0 NormalZ=1 AngleXU=0 Radius=3.6 StartAngle=0.698132 EndAngle=3.14159
    g1: ArcOfCircle CenterX=0 CenterY=0 CenterZ=0 NormalX=0 NormalY=0 NormalZ=1 AngleXU=0 Radius=7.6 StartAngle=0.698132 EndAngle=3.14159
    g2: LineSegment StartX=-7.6 StartY=9e-16 StartZ=0 EndX=-3.6 EndY=4e-16 EndZ=0
    g3: LineSegment StartX=2.75776 StartY=2.31404 StartZ=0 EndX=5.82194 EndY=4.88519 EndZ=0
  constraints (12):
    c: Coincident(g0,g-1)
    c: PointOnObject(g0,g-1)
    c: Coincident(g1,g0)
    c: PointOnObject(g1,g-1)
    c: Coincident(g2,g1)
    c: Coincident(g2,g0)
    c: Coincident(g3,g0)
    c: Coincident(g3,g1)
    c: PointOnObject(g0,g3)
    c: Diameter(g0) = 7.2
    c: Diameter(g1) = 15.2
    c: Angle(g3) = 0.698132
FEATURE [PartDesign::Pad] Pad
  Direction = (0,0,1)
  Length = 1.3
  Length2 = 10
  Profile = -> Sketch002
  ReferenceAxis = -> Sketch002 [N_Axis]
  Suppressed = false
  Type = 0
FEATURE [PartDesign::Mirrored] Mirrored001
  BaseFeature = -> Pad
  MirrorPlane = -> Sketch002 [H_Axis]
  Originals = -> [Pad]
  Suppressed = false
FEATURE [PartDesign::AdditiveTorus] Torus
  Angle1 = -180
  Angle2 = 180
  Angle3 = 360
  AttacherType = Attacher::AttachEngine3D
  Radius1 = 7
  Radius2 = 2
  Suppressed = false
FEATURE [Sketcher::SketchObject] Sketch003
  AttachmentSupport = -> [XY_Plane004]
  FullyConstrained = true
  MapMode = 5
  sketch-geometry (7):
    g0: LineSegment StartX=7.73649 StartY=0 StartZ=0 EndX=3.86825 EndY=6.7 EndZ=0
    g1: LineSegment StartX=3.86825 StartY=6.7 StartZ=0 EndX=-3.86825 EndY=6.7 EndZ=0
    g2: LineSegment StartX=-3.86825 StartY=6.7 StartZ=0 EndX=-7.73649 EndY=-1.13589e-11 EndZ=0
    g3: LineSegment StartX=-7.73649 StartY=-1.13592e-11 StartZ=0 EndX=-3.86825 EndY=-6.7 EndZ=0
    g4: LineSegment StartX=-3.86825 StartY=-6.7 StartZ=0 EndX=3.86825 EndY=-6.7 EndZ=0
    g5: LineSegment StartX=3.86825 StartY=-6.7 StartZ=0 EndX=7.73649 EndY=0 EndZ=0
    g6: Circle CenterX=0 CenterY=0 CenterZ=0 NormalX=0 NormalY=0 NormalZ=1 AngleXU=0 Radius=7.73649
  constraints (16):
    c: Coincident(g0,g1)
    c: Coincident(g1,g2)
    c: Coincident(g2,g3)
    c: Coincident(g3,g4)
    c: Coincident(g4,g5)
    c: Coincident(g5,g0)
    c: Equal(g0, g1-g5) x5
    c: PointOnObject(g0,g6)
    c: PointOnObject(g1,g6)
    c: PointOnObject(g2,g6)
    c: PointOnObject(g3,g6)
    c: PointOnObject(g4,g6)
    c: PointOnObject(g5,g6)
    c: Coincident(g6,g-1)
    c: PointOnObject(g5,g-1)
    c: DistanceY(g4,g0) = 13.4
FEATURE [Sketcher::SketchObject] Sketch004
  AttachmentSupport = -> [XY_Plane004]
  FullyConstrained = true
  MapMode = 5
  sketch-geometry (1):
    g0: Circle CenterX=0 CenterY=0 CenterZ=0 NormalX=0 NormalY=0 NormalZ=1 AngleXU=0 Radius=8.4
  constraints (2):
    c: Coincident(g0,g-1)
    c: Diameter(g0) = 16.8
FEATURE [PartDesign::Pad] Pad001
  Direction = (0,0,1)
  Length = 6
  Length2 = 10
  Profile = -> Sketch003
  ReferenceAxis = -> Sketch003 [N_Axis]
  Suppressed = false
  Type = 0
FEATURE [PartDesign::Pad] Pad002
  BaseFeature = -> Pad001
  Direction = (0,0,1)
  Length = 1
  Length2 = 10
  Profile = -> Sketch004
  ReferenceAxis = -> Sketch004 [N_Axis]
  Suppressed = false
  Type = 0
FEATURE [Sketcher::SketchObject] Sketch005
  AttachmentSupport = -> [XY_Plane004]
  FullyConstrained = true
  MapMode = 5
  sketch-geometry (1):
    g0: Circle CenterX=0 CenterY=0 CenterZ=0 NormalX=0 NormalY=0 NormalZ=1 AngleXU=0 Radius=4.625
  constraints (2):
    c: Coincident(g0,g-1)
    c: Diameter(g0) = 9.25
FEATURE [PartDesign::Pocket] Pocket
  BaseFeature = -> Pad002
  Direction = (0,0,-1)
  Length = 5
  Length2 = 5
  Midplane = true
  Profile = -> Sketch005
  ReferenceAxis = -> Sketch005 [N_Axis]
  Suppressed = false
  Type = 1
FEATURE [PartDesign::CoordinateSystem] Local_CS
  AttacherType = Attacher::AttachEngine3D
  AttachmentSupport = -> [XY_Plane]
  MapMode = 5
FEATURE [PartDesign::Body] Body
  Group = -> [Sketch,Revolution,Mirrored,Local_CS]
  Origin = -> Origin
  Tip = -> Mirrored
FEATURE [PartDesign::CoordinateSystem] Local_CS001
  AttacherType = Attacher::AttachEngine3D
  AttachmentOffset = pos=(0,0,2) rot=(0,0,1;0rad)
  AttachmentSupport = -> [XY_Plane001]
  MapMode = 5
  Placement = pos=(0,0,2) rot=(0,0,1;0rad)
FEATURE [PartDesign::CoordinateSystem] Local_CS002
  AttacherType = Attacher::AttachEngine3D
  AttachmentOffset = pos=(0,0,16) rot=(0,0,1;0rad)
  AttachmentSupport = -> [XY_Plane001]
  MapMode = 5
  Placement = pos=(0,0,16) rot=(0,0,1;0rad)
FEATURE [PartDesign::CoordinateSystem] Local_CS003
  AttacherType = Attacher::AttachEngine3D
  AttachmentOffset = pos=(0,0,55) rot=(0,0,1;0rad)
  AttachmentSupport = -> [XY_Plane001]
  MapMode = 5
  Placement = pos=(0,0,55) rot=(0,0,1;0rad)
FEATURE [PartDesign::CoordinateSystem] Local_CS004
  AttacherType = Attacher::AttachEngine3D
  AttachmentOffset = pos=(0,0,57) rot=(0,0,1;0rad)
  AttachmentSupport = -> [XY_Plane001]
  MapMode = 5
  Placement = pos=(0,0,57) rot=(0,0,1;0rad)
FEATURE [PartDesign::Body] Body001
  Group = -> [Sketch001,Revolution001,Local_CS001,Local_CS002,Local_CS003,Local_CS004]
  Origin = -> Origin001
  Tip = -> Revolution001
FEATURE [PartDesign::CoordinateSystem] Local_CS005
  AttacherType = Attacher::AttachEngine3D
  AttachmentSupport = -> [XY_Plane002]
  MapMode = 5
FEATURE [PartDesign::Body] Body002
  Group = -> [Sketch002,Pad,Mirrored001,Local_CS005]
  Origin = -> Origin002
  Tip = -> Mirrored001
FEATURE [PartDesign::CoordinateSystem] Local_CS006
  AttacherType = Attacher::AttachEngine3D
  AttachmentSupport = -> [XY_Plane003]
  MapMode = 5
FEATURE [PartDesign::Body] Body003
  Group = -> [Torus,Local_CS006]
  Origin = -> Origin003
  Tip = -> Torus
FEATURE [PartDesign::CoordinateSystem] Local_CS007
  AttacherType = Attacher::AttachEngine3D
  AttachmentSupport = -> [XY_Plane004]
  MapMode = 5
FEATURE [PartDesign::Body] Body004
  Group = -> [Sketch003,Sketch004,Pad001,Pad002,Sketch005,Pocket,Local_CS007]
  Origin = -> Origin004
  Tip = -> Pocket
FEATURE [App::Link] Body005
  LinkedObject = -> Body001
FEATURE [App::Part] Part_Body001  label="Part_Body001 🔒 "
  Group = -> [Body005]
  Origin = -> Origin006
  Placement = pos=(0,0,-52) rot=(0,0,1;0rad)
FEATURE [App::Link] Body006
  LinkedObject = -> Body
FEATURE [App::Part] Part_Body
  Group = -> [Body006]
  Origin = -> Origin007
  Placement = pos=(0,0,-36) rot=(0,0,1;0rad)
FEATURE [App::Link] Body007
  LinkedObject = -> Body002
FEATURE [App::Part] Part_Body002
  Group = -> [Body007]
  Origin = -> Origin008
  Placement = pos=(0,0,-50) rot=(0,0,1;0rad)
FEATURE [App::Link] Body008
  LinkedObject = -> Body003
FEATURE [App::Part] Part_Body003
  Group = -> [Body008]
  Origin = -> Origin009
  Placement = pos=(0,0,3) rot=(0,0,1;0rad)
FEATURE [App::Link] Body009
  LinkedObject = -> Body004
FEATURE [App::Part] Part_Body004
  Group = -> [Body009]
  Origin = -> Origin010
  Placement = pos=(0,0,5) rot=(0,0,1;0rad)
FEATURE [App::FeaturePython] Fixed  # Assembly joint (typed FeaturePython)
  Activated = true
  Detach1 = false
  Detach2 = false
  Distance = 0
  JointType = 0 (Fixed)
  Object1 = Local_CS001
  Object2 = Local_CS005
  Offset = (0,0,0)
  Part1 = -> Part_Body001
  Part2 = -> Part_Body002
  Rotation = 0
FEATURE [App::FeaturePython] Fixed001  # Assembly joint (typed FeaturePython)
  Activated = true
  Detach1 = false
  Detach2 = false
  Distance = 0
  JointType = 0 (Fixed)
  Object1 = Local_CS003
  Object2 = Local_CS006
  Offset = (0,0,0)
  Part1 = -> Part_Body001
  Part2 = -> Part_Body003
  Rotation = 0
FEATURE [App::FeaturePython] Fixed002  # Assembly joint (typed FeaturePython)
  Activated = true
  Detach1 = false
  Detach2 = false
  Distance = 0
  JointType = 0 (Fixed)
  Object1 = Local_CS004
  Object2 = Local_CS007
  Offset = (0,0,0)
  Part1 = -> Part_Body001
  Part2 = -> Part_Body004
  Rotation = 0
FEATURE [App::FeaturePython] GroundedJoint  # Assembly grounded joint (typed FeaturePython)
  ObjectToGround = -> Part_Body001
  Placement = pos=(0,0,-52) rot=(0,0,1;0rad)
FEATURE [App::FeaturePython] Fixed003  # Assembly joint (typed FeaturePython)
  Activated = true
  Detach1 = false
  Detach2 = false
  Distance = 0
  JointType = 0 (Fixed)
  Object1 = Local_CS002
  Object2 = Local_CS
  Offset = (0,0,0)
  Part1 = -> Part_Body001
  Part2 = -> Part_Body
  Rotation = 0
FEATURE [Assembly::JointGroup] Joints
  Group = -> [Fixed,Fixed001,Fixed002,GroundedJoint,Fixed003]
FEATURE [PartDesign::CoordinateSystem] Local_CS008
  AttacherType = Attacher::AttachEngine3D
  AttachmentSupport = -> [XY_Plane005]
  MapMode = 5
FEATURE [Assembly::AssemblyObject] Assembly
  Group = -> [Joints,Part_Body001,Part_Body,Part_Body002,Part_Body003,Part_Body004,Fixed,Fixed001,Fixed002,GroundedJoint,Fixed003,Local_CS008]
  Origin = -> Origin005
  Type = Assembly
FEATURE [Part::FeaturePython] aCircle  # WARN: FeaturePython — macro-defined, semantics opaque (R4)
FEATURE [Part::FeaturePython] Radius  # WARN: FeaturePython — macro-defined, semantics opaque (R4)
FEATURE [App::AnnotationLabel] MeasureLbl
  BasePosition = (4.9,1.48e-14,14.6)
  LabelText = R = 4,9000 mm
  TextPosition = (0,0,0)
FEATURE [Part::FeaturePython] aCircle001  # WARN: FeaturePython — macro-defined, semantics opaque (R4)
FEATURE [Part::FeaturePython] Radius001  # WARN: FeaturePython — macro-defined, semantics opaque (R4)
FEATURE [App::AnnotationLabel] MeasureLbl001
  BasePosition = (8.4,0,6)
  LabelText = R = 8,4000 mm
  TextPosition = (0,0,0)
FEATURE [App::DocumentObjectGroup] Measures
  Group = -> [aCircle,Radius,MeasureLbl,aCircle001,Radius001,MeasureLbl001]
---- part composit_stand10.FCStd = doc fcstd_435c06b994c1 (352267 chars; too large to inline — full recipe in that document) ----
